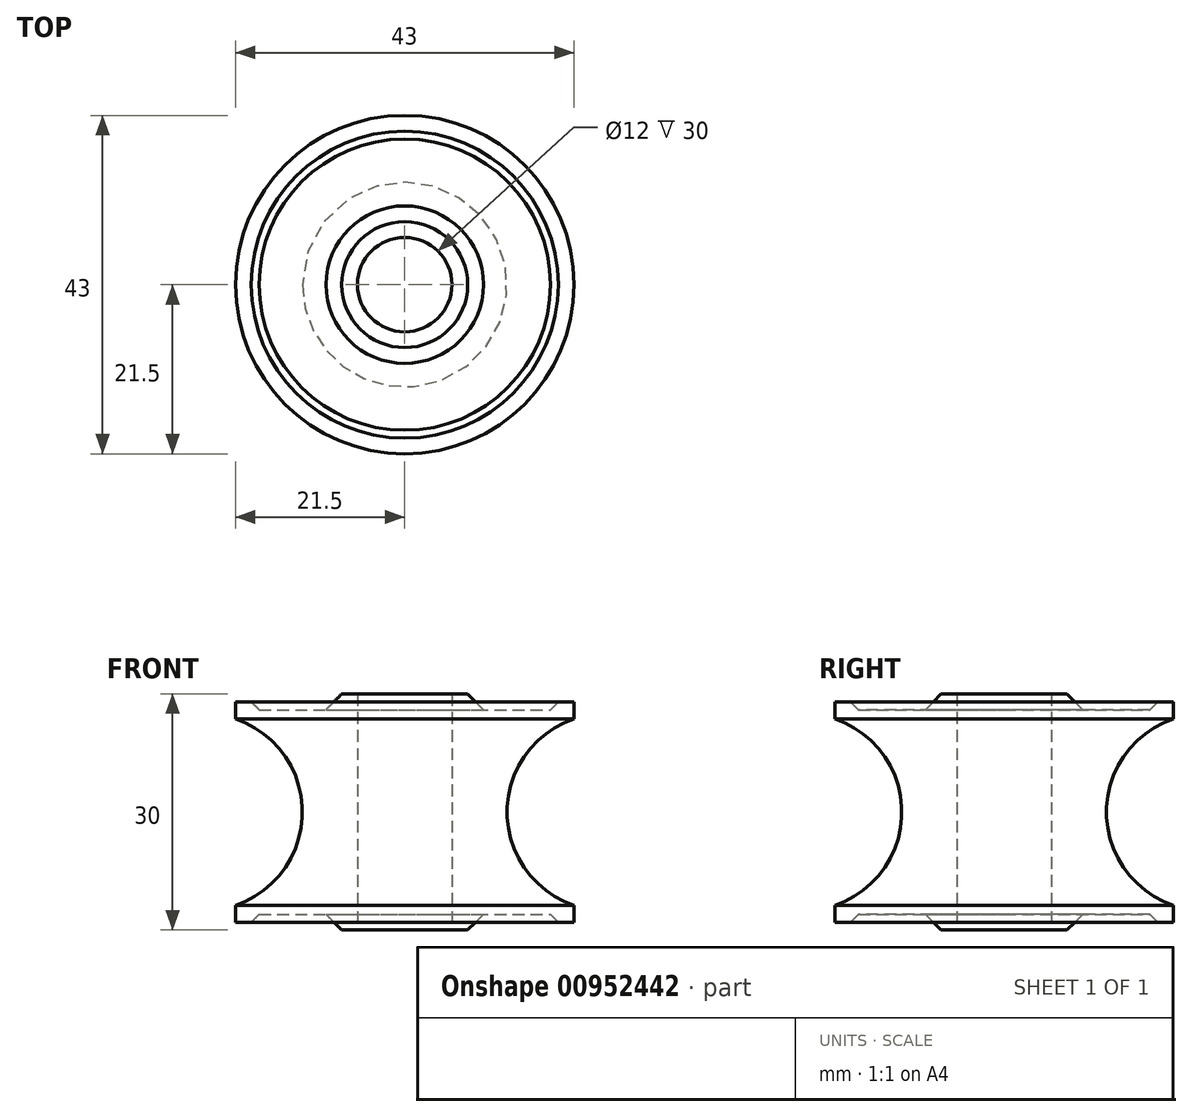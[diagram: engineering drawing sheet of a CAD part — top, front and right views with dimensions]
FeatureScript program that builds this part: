
annotation { "Feature Type Name" : "Feature", "Feature Type Description" : "" }
export const myFeature = defineFeature(function(context is Context, id is Id, definition is map)
    precondition{}
    {
        {
            var Q0;
            Q0=qCreatedBy(makeId("Front.planeOp"),FACE);
            var sketch = newSketch(context, id + "F0", { "sketchPlane" : qUnion([Q0])});
            skLineSegment(sketch, "E0", {"start": v(0, 0) * mm, "end": v(0, 45.47) * mm, "construction": true});
            skLineSegment(sketch, "E1", {"start": v(6, 30) * mm, "end": v(6, 0) * mm});
            skLineSegment(sketch, "E2", {"start": v(6, 0) * mm, "end": v(8, 0) * mm});
            skLineSegment(sketch, "E3", {"start": v(8, 0) * mm, "end": v(10, 2) * mm});
            skLineSegment(sketch, "E4", {"start": v(10, 2) * mm, "end": v(18.5, 2) * mm});
            skLineSegment(sketch, "E5", {"start": v(21.5, 1) * mm, "end": v(21.5, 3.16) * mm});
            skLineSegment(sketch, "E6", {"start": v(13, 15) * mm, "end": v(13, 15) * mm});
            skLineSegment(sketch, "E7", {"start": v(19.5, 29) * mm, "end": v(18.5, 28) * mm});
            skLineSegment(sketch, "E8", {"start": v(18.5, 28) * mm, "end": v(10, 28) * mm});
            skLineSegment(sketch, "E9", {"start": v(10, 28) * mm, "end": v(8, 30) * mm});
            skLineSegment(sketch, "E10", {"start": v(8, 30) * mm, "end": v(6, 30) * mm});
            skLineSegment(sketch, "E11", {"start": v(18.5, 2) * mm, "end": v(19.5, 1) * mm});
            skLineSegment(sketch, "E12", {"start": v(19.5, 1) * mm, "end": v(21.5, 1) * mm});
            skLineSegment(sketch, "E13", {"start": v(21.5, 26.84) * mm, "end": v(21.5, 29) * mm});
            skLineSegment(sketch, "E14", {"start": v(21.5, 29) * mm, "end": v(19.5, 29) * mm});
            skLineSegment(sketch, "E15", {"start": v(6, 15) * mm, "end": v(31.65, 15) * mm, "construction": true});
            skPoint(sketch, "E16.visualSharp", {"position": v(13, 27.5) * mm});
            skArc(sketch, "E16.filletArc", {"start": v(21.5, 26.84) * mm, "mid": v(15.34, 22.29) * mm, "end": v(13, 15) * mm});
            skPoint(sketch, "E17.visualSharp", {"position": v(13, 3.25) * mm});
            skArc(sketch, "E17.filletArc", {"start": v(13, 15) * mm, "mid": v(15.34, 7.71) * mm, "end": v(21.5, 3.16) * mm});
            skSolve(sketch);
        }
        {
            var Q0;
            Q0=makeQuery(id+"F0.imprint","IMPRINT",FACE,{"disambiguationData":[TD([[makeQuery(id+"F0.imprint","IMPRINT",EDGE,{"derivedFrom":sQuery(id+"F0.wireOp",EDGE,"E1")}),1.0]])]});
            var Q1;
            Q1=sQuery(id+"F0.wireOp",EDGE,"E0");
            revolve(context, id + "F1", {"surfaceOperationType" : NewSurfaceOperationType.NEW, "entities" : qUnion([Q0]), "axis" : qUnion([Q1]), "revolveType" : RevolveType.FULL});
        }
    });
